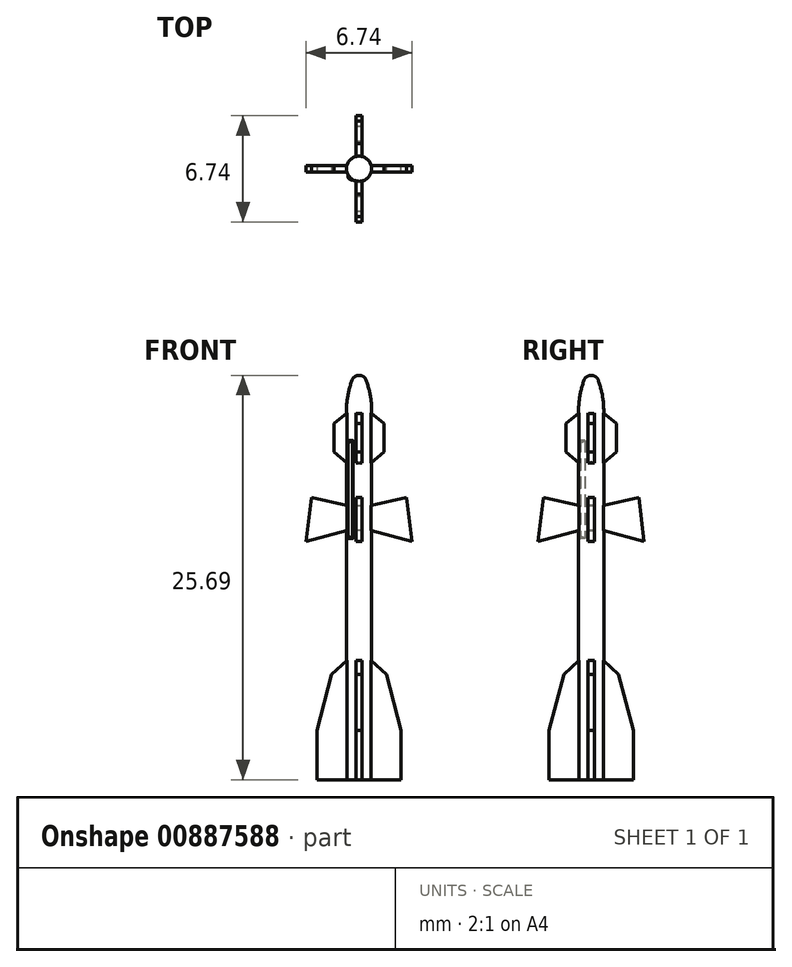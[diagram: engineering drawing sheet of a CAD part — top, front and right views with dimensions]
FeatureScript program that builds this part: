
annotation { "Feature Type Name" : "Feature", "Feature Type Description" : "" }
export const myFeature = defineFeature(function(context is Context, id is Id, definition is map)
    precondition{}
    {
        {
            assignVariable(context, id + "F0", {"name" : "s", "anyValue" : 144});
        }
        {
            var Q0;
            Q0=qCreatedBy(makeId("Front.planeOp"),FACE);
            var sketch = newSketch(context, id + "F1", { "sketchPlane" : qUnion([Q0])});
            skLineSegment(sketch, "E0", {"start": v(0, 0) * mm, "end": v(0, 25.7) * mm});
            skLineSegment(sketch, "E1", {"start": v(0.8, 23.44) * mm, "end": v(0.8, 0) * mm});
            skLineSegment(sketch, "E2", {"start": v(0.8, 0) * mm, "end": v(0, 0) * mm});
            skArc(sketch, "E3", {"start": v(0.45, 25.38) * mm, "mid": v(0.27, 25.6) * mm, "end": v(0, 25.7) * mm});
            skLineSegment(sketch, "E4", {"start": v(0, 25.7) * mm, "end": v(6.02, 25.7) * mm, "construction": true});
            skArc(sketch, "E5", {"start": v(0.8, 23.44) * mm, "mid": v(0.71, 24.43) * mm, "end": v(0.45, 25.38) * mm});
            skSolve(sketch);
        }
        {
            var Q0;
            Q0 = qSketchRegion(id + "F1", true);
            var Q1;
            Q1=sQuery(id+"F1.wireOp",EDGE,"E0");
            revolve(context, id + "F2", {"surfaceOperationType" : NewSurfaceOperationType.NEW, "entities" : qUnion([Q0]), "axis" : qUnion([Q1]), "revolveType" : RevolveType.FULL});
        }
        {
            var Q0;
            Q0=qCreatedBy(makeId("Front.planeOp"),FACE);
            var sketch = newSketch(context, id + "F3", { "sketchPlane" : qUnion([Q0])});
            skLineSegment(sketch, "E6", {"start": v(0, 0) * mm, "end": v(0, 23.89) * mm});
            skLineSegment(sketch, "E7", {"start": v(0, 23.89) * mm, "end": v(1.6, 22.64) * mm});
            skLineSegment(sketch, "E8", {"start": v(1.6, 22.64) * mm, "end": v(1.6, 20.83) * mm});
            skLineSegment(sketch, "E9", {"start": v(1.6, 20.83) * mm, "end": v(0.4, 19.8) * mm});
            skLineSegment(sketch, "E10", {"start": v(0.4, 19.8) * mm, "end": v(0.4, 17.34) * mm});
            skLineSegment(sketch, "E11", {"start": v(0.4, 17.34) * mm, "end": v(3.02, 17.92) * mm});
            skLineSegment(sketch, "E12", {"start": v(3.02, 17.92) * mm, "end": v(3.37, 15.14) * mm});
            skLineSegment(sketch, "E13", {"start": v(3.37, 15.14) * mm, "end": v(0.4, 15.94) * mm});
            skLineSegment(sketch, "E14", {"start": v(0.4, 15.94) * mm, "end": v(0.4, 7.94) * mm});
            skLineSegment(sketch, "E15", {"start": v(0.4, 7.94) * mm, "end": v(1.74, 6.7) * mm});
            skLineSegment(sketch, "E16", {"start": v(1.74, 6.7) * mm, "end": v(2.67, 3.12) * mm});
            skLineSegment(sketch, "E17", {"start": v(2.67, 3.12) * mm, "end": v(2.67, 0) * mm});
            skLineSegment(sketch, "E18", {"start": v(2.67, 0) * mm, "end": v(0, 0) * mm});
            skLineSegment(sketch, "E19.0", {"start": v(0.8, 0) * mm, "end": v(-0.8, 0) * mm});
            skLineSegment(sketch, "E20", {"start": v(0.8, 0) * mm, "end": v(0.8, 32.87) * mm, "construction": true});
            skPoint(sketch, "E21", {"position": v(0.8, 7.57) * mm});
            skPoint(sketch, "E22", {"position": v(0.8, 15.83) * mm});
            skPoint(sketch, "E23", {"position": v(0.8, 17.43) * mm});
            skPoint(sketch, "E24", {"position": v(0.8, 20.14) * mm});
            skPoint(sketch, "E25", {"position": v(0.8, 23.26) * mm});
            skSolve(sketch);
        }
        {
            var Q0;
            Q0 = qSketchRegion(id + "F3", true);
            extrude(context, id + "F4", {"entities" : qUnion([Q0]), "operationType" : NewBodyOperationType.ADD, "depth" : .4 * mm, "offsetDistance" : 25 * mm, "symmetric" : true});
        }
        {
            var Q0;
            Q0=makeQuery(id+"F2.opRevolve","SWEPT_BODY",BODY,{"disambiguationData":[OSD([sQuery(id+"F1.wireOp",EDGE,"E0"),sQuery(id+"F1.wireOp",EDGE,"E1"),sQuery(id+"F1.wireOp",EDGE,"E2"),sQuery(id+"F1.wireOp",EDGE,"E3"),sQuery(id+"F1.wireOp",EDGE,"E5")])]});
            var Q1;
            Q1=makeQuery(id+"F2.opRevolve","SWEPT_FACE",FACE,{"disambiguationData":[OSD([sQuery(id+"F1.wireOp",EDGE,"E1")])]});
            circularPattern(context, id + "F5", {"operationType" : NewBodyOperationType.ADD, "entities" : qUnion([Q0]), "axis" : qUnion([Q1]), "angle" : 360 * degree, "instanceCount" : 4, "equalSpace" : true, "computeTransformsWithoutBuiltin" : true});
        }
        {
            var Q0;
            Q0=qCreatedBy(makeId("Top.planeOp"),FACE);
            cPlane(context, id + "F6", {"entities" : qUnion([Q0]), "cplaneType" : CPlaneType.OFFSET, "offset" : (2220 / getVariable(context, 's')) * mm, "width" : 150 * mm, "height" : 150 * mm});
        }
        {
            var Q0;
            Q0=qCreatedBy(id+"F6.planeOp",FACE);
            var sketch = newSketch(context, id + "F7", { "sketchPlane" : qUnion([Q0])});
            skLineSegment(sketch, "E26", {"start": v(-0.14, -0.44) * mm, "end": v(-0.44, -0.14) * mm});
            skLineSegment(sketch, "E27", {"start": v(-0.44, -0.14) * mm, "end": v(-0.7, -0.4) * mm});
            skLineSegment(sketch, "E28", {"start": v(-0.4, -0.7) * mm, "end": v(-0.14, -0.44) * mm});
            skLineSegment(sketch, "E29", {"start": v(0, -0.64) * mm, "end": v(0, 0) * mm, "construction": true});
            skLineSegment(sketch, "E30", {"start": v(0, 0) * mm, "end": v(-0.29, -0.29) * mm, "construction": true});
            skArc(sketch, "E31", {"start": v(-0.7, -0.4) * mm, "mid": v(-0.64, -0.64) * mm, "end": v(-0.4, -0.7) * mm});
            skSolve(sketch);
        }
        {
            var Q0;
            Q0 = qSketchRegion(id + "F7", true);
            extrude(context, id + "F8", {"entities" : qUnion([Q0]), "operationType" : NewBodyOperationType.ADD, "depth" : (870 / getVariable(context, 's')) * mm, "offsetDistance" : 25 * mm});
        }
        {
            var Q0;
            Q0=makeQuery(id+"F8.boolean.opBoolean","INTERSECT",EDGE,{"derivedFrom":[makeQuery(id+"F2.opRevolve","SWEPT_FACE",FACE,{"disambiguationData":[OSD([sQuery(id+"F1.wireOp",EDGE,"E1")])]}),makeQuery(id+"F8.opExtrude","CAP_FACE",FACE,{"disambiguationData":[OSD([sQuery(id+"F7.wireOp",EDGE,"E26"),sQuery(id+"F7.wireOp",EDGE,"E27"),sQuery(id+"F7.wireOp",EDGE,"E28"),sQuery(id+"F7.wireOp",EDGE,"E31")])],"isStart":false})]});
            var Q1;
            Q1=makeQuery(id+"F8.boolean.opBoolean","INTERSECT",EDGE,{"derivedFrom":[makeQuery(id+"F2.opRevolve","SWEPT_FACE",FACE,{"disambiguationData":[OSD([sQuery(id+"F1.wireOp",EDGE,"E1")])]}),makeQuery(id+"F8.opExtrude","CAP_FACE",FACE,{"disambiguationData":[OSD([sQuery(id+"F7.wireOp",EDGE,"E26"),sQuery(id+"F7.wireOp",EDGE,"E27"),sQuery(id+"F7.wireOp",EDGE,"E28"),sQuery(id+"F7.wireOp",EDGE,"E31")])],"isStart":true})]});
            chamfer(context, id + "F9", {"entities" : qUnion([Q0, Q1]), "width" : .1 * mm, "tangentPropagation" : true});
        }
    });
